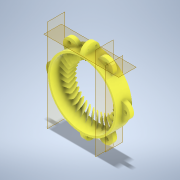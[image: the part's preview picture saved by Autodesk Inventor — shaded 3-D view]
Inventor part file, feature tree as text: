
AUTODESK INVENTOR PART (.ipt)
format: ipt  version: 2021.2 (Build 252289000, 289)  size: 952,320 bytes
history: native  units: in
note: dims shown in document units (in); Inventor stores cm internally (conversion verified against a paired STEP export)
features: sketch x9, extrude x8, plane x4, pattern_circular x3, fillet x2, loft x1, other x1
ambient origin geometry x8: Origin, YZ Plane, XZ Plane, XY Plane, X Axis, Y Axis, Z Axis, Center Point
bodies: Solid1 (feature_tree)
feature tree (28):
  extrude  "Extrusion1"  Depth=4.25in
  plane  "Work Plane1"
  plane  "Work Plane2"
  extrude  "Extrusion3"  Depth=1.5in
  fillet  "Fillet1"  Radius=2.125in
  extrude  "Extrusion4"  TaperAngle=0.0deg  [1 undecoded]
  pattern_circular  "Circular Pattern2"  Count=2 Angle=360.0deg
  plane  "Work Plane3"
  extrude  "Extrusion5"  Depth=1.0in
  extrude  "Extrusion6"  Depth=0.25in
  fillet  "Fillet2"  Radius=0.5in
  extrude  "Extrusion7"  TaperAngle=0.0deg  [1 undecoded]
  pattern_circular  "Circular Pattern3"  [2 undecoded]
  extrude  "Extrusion8"  Depth=0.5in TaperAngle=0.0deg
  plane  "Work Plane4"
  loft  "Loft1"
  pattern_circular  "Circular Pattern5"  [2 undecoded]
  extrude  "Extrusion9"  Depth=0.2in
  sketch  "Sketch1"  dims[d0=4.0in d1=4.25in]
  sketch  "Sketch3"  dims[d2=1.0in d3=0.0in d4=1.5in d10=2.125in]
  sketch  "Sketch4"  dims[d11=0.25in d12=0.0in]
  sketch  "Sketch5"  dims[d13=0.5in d14=0.0in]
  sketch  "Sketch6"  dims[d15=0.5in]
  sketch  "Sketch7"  dims[d16=0.125in]
  sketch  "Sketch8"  dims[d17=0.2in]
  sketch  "Sketch9"  dims[d18=0.5in d19=0.0in d20=0.7874in d21=360.0deg]
  other  "Edges1"
  sketch  "Sketch10"  dims[d23=-2.125in d24=1.0in d25=0.25in d26=0.5in d27=0.0in d28=0.1in d29=0.0in d30=0.5in d31=0.0in d32=0.5in d33=0.25in d34=0.2in d35=0.5in d36=0.0in d37=2.3622in d38=360.0deg d40=0.25in d41=0.125in d42=0.25in d43=0.2in d49=0.5in d50=0.0312in d51=0.5in d52=0.0in d56=0.9in d57=0.0in d58=90.0deg d59=0.0in d60=90.0deg d61=14.1732in d62=360.0deg d64=2.6625in d65=0.0in d66=0.0777in]
note: 6 required parameter values undecoded (feature->parameter linkage not recoverable at this tier; creation-order binding heuristic only, values carry confidence <= 0.55)
